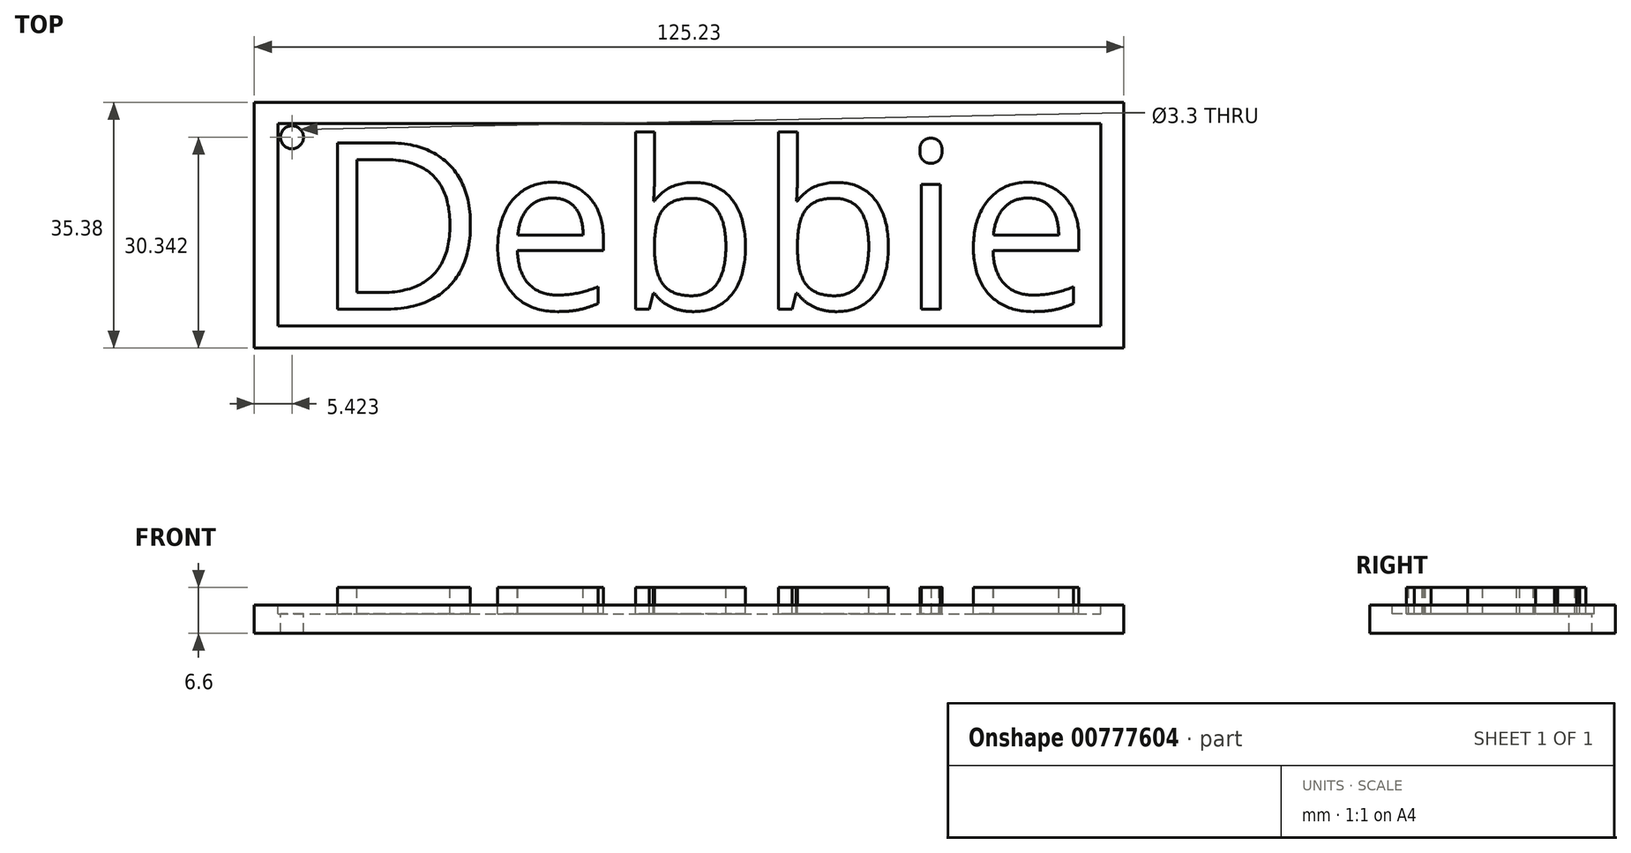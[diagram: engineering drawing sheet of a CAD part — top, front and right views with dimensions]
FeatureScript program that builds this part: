
annotation { "Feature Type Name" : "Feature", "Feature Type Description" : "" }
export const myFeature = defineFeature(function(context is Context, id is Id, definition is map)
    precondition{}
    {
        {
            var Q0;
            Q0=qCreatedBy(makeId("Top.planeOp"),FACE);
            var sketch = newSketch(context, id + "F0", { "sketchPlane" : qUnion([Q0])});
            skLineSegment(sketch, "E0.bottom", {"start": v(-61.28, 18.72) * mm, "end": v(63.95, 18.72) * mm});
            skLineSegment(sketch, "E0.top", {"start": v(-61.28, -16.66) * mm, "end": v(63.95, -16.66) * mm});
            skLineSegment(sketch, "E0.left", {"start": v(-61.28, 18.72) * mm, "end": v(-61.28, -16.66) * mm});
            skLineSegment(sketch, "E0.right", {"start": v(63.95, 18.72) * mm, "end": v(63.95, -16.66) * mm});
            skSolve(sketch);
        }
        {
            var Q0;
            Q0 = qSketchRegion(id + "F0", true);
            extrude(context, id + "F1", {"entities" : qUnion([Q0]), "depth" : 4.06 * mm, "offsetDistance" : 25.4 * mm});
        }
        {
            var Q0;
            Q0=makeQuery(id+"F1.opExtrude","CAP_FACE",FACE,{"disambiguationData":[OSD([sQuery(id+"F0.wireOp",EDGE,"E0.bottom"),sQuery(id+"F0.wireOp",EDGE,"E0.top"),sQuery(id+"F0.wireOp",EDGE,"E0.left"),sQuery(id+"F0.wireOp",EDGE,"E0.right")])],"isStart":false});
            var sketch = newSketch(context, id + "F2", { "sketchPlane" : qUnion([Q0])});
            skLineSegment(sketch, "E1.bottom", {"start": v(-57.9, 15.63) * mm, "end": v(60.65, 15.63) * mm});
            skLineSegment(sketch, "E1.top", {"start": v(-57.9, -13.47) * mm, "end": v(60.65, -13.47) * mm});
            skLineSegment(sketch, "E1.left", {"start": v(-57.9, 15.63) * mm, "end": v(-57.9, -13.47) * mm});
            skLineSegment(sketch, "E1.right", {"start": v(60.65, 15.63) * mm, "end": v(60.65, -13.47) * mm});
            skSolve(sketch);
        }
        {
            var Q0;
            Q0 = qSketchRegion(id + "F2", true);
            extrude(context, id + "F3", {"entities" : qUnion([Q0]), "operationType" : NewBodyOperationType.REMOVE, "oppositeDirection" : true, "depth" : 1.27 * mm, "offsetDistance" : 25.4 * mm});
        }
        {
            var Q0;
            Q0=makeQuery(id+"F2.imprint","IMPRINT",FACE,{"disambiguationData":[TD([[makeQuery(id+"F2.imprint","IMPRINT",EDGE,{"derivedFrom":sQuery(id+"F2.wireOp",EDGE,"E1.bottom")}),-1.0]])]});
            var sketch = newSketch(context, id + "F4", { "sketchPlane" : qUnion([Q0])});
            skText(sketch, "E2", { "text": "Debbie\n", "fontName": "OpenSans-Regular.ttf"});
            const initialGuessF4  = {"E2": [-0.05259, -0.0111, 1, 0, 0.02418]};
            skSetInitialGuess(sketch, initialGuessF4);
            skSolve(sketch);
        }
        {
            var Q0;
            Q0 = qSketchRegion(id + "F4", true);
            extrude(context, id + "F5", {"entities" : qUnion([Q0]), "operationType" : NewBodyOperationType.ADD, "oppositeDirection" : true, "depth" : 4.06 * mm, "offsetDistance" : 25.4 * mm});
        }
        {
            var Q0;
            Q0=makeQuery(id+"F2.imprint","IMPRINT",FACE,{"disambiguationData":[TD([[makeQuery(id+"F2.imprint","IMPRINT",EDGE,{"derivedFrom":sQuery(id+"F2.wireOp",EDGE,"E1.bottom")}),-1.0]])]});
            var sketch = newSketch(context, id + "F6", { "sketchPlane" : qUnion([Q0])});
            skCircle(sketch, "E3", {"center": v(-55.86, 13.68) * mm, "radius": 1.65 * mm});
            skSolve(sketch);
        }
        {
            var Q0;
            Q0 = qSketchRegion(id + "F6", true);
            extrude(context, id + "F7", {"entities" : qUnion([Q0]), "operationType" : NewBodyOperationType.REMOVE, "oppositeDirection" : true, "depth" : 25.4 * mm, "offsetDistance" : 25.4 * mm});
        }
        {
            var Q0;
            Q0 = qSketchRegion(id + "F4", true);
            extrude(context, id + "F8", {"entities" : qUnion([Q0]), "operationType" : NewBodyOperationType.ADD, "depth" : 1.27 * mm, "offsetDistance" : 25.4 * mm});
        }
        {
            var Q0;
            Q0 = qSketchRegion(id + "F4", true);
            extrude(context, id + "F9", {"entities" : qUnion([Q0]), "operationType" : NewBodyOperationType.ADD, "depth" : 2.54 * mm, "offsetDistance" : 25.4 * mm});
        }
    });
